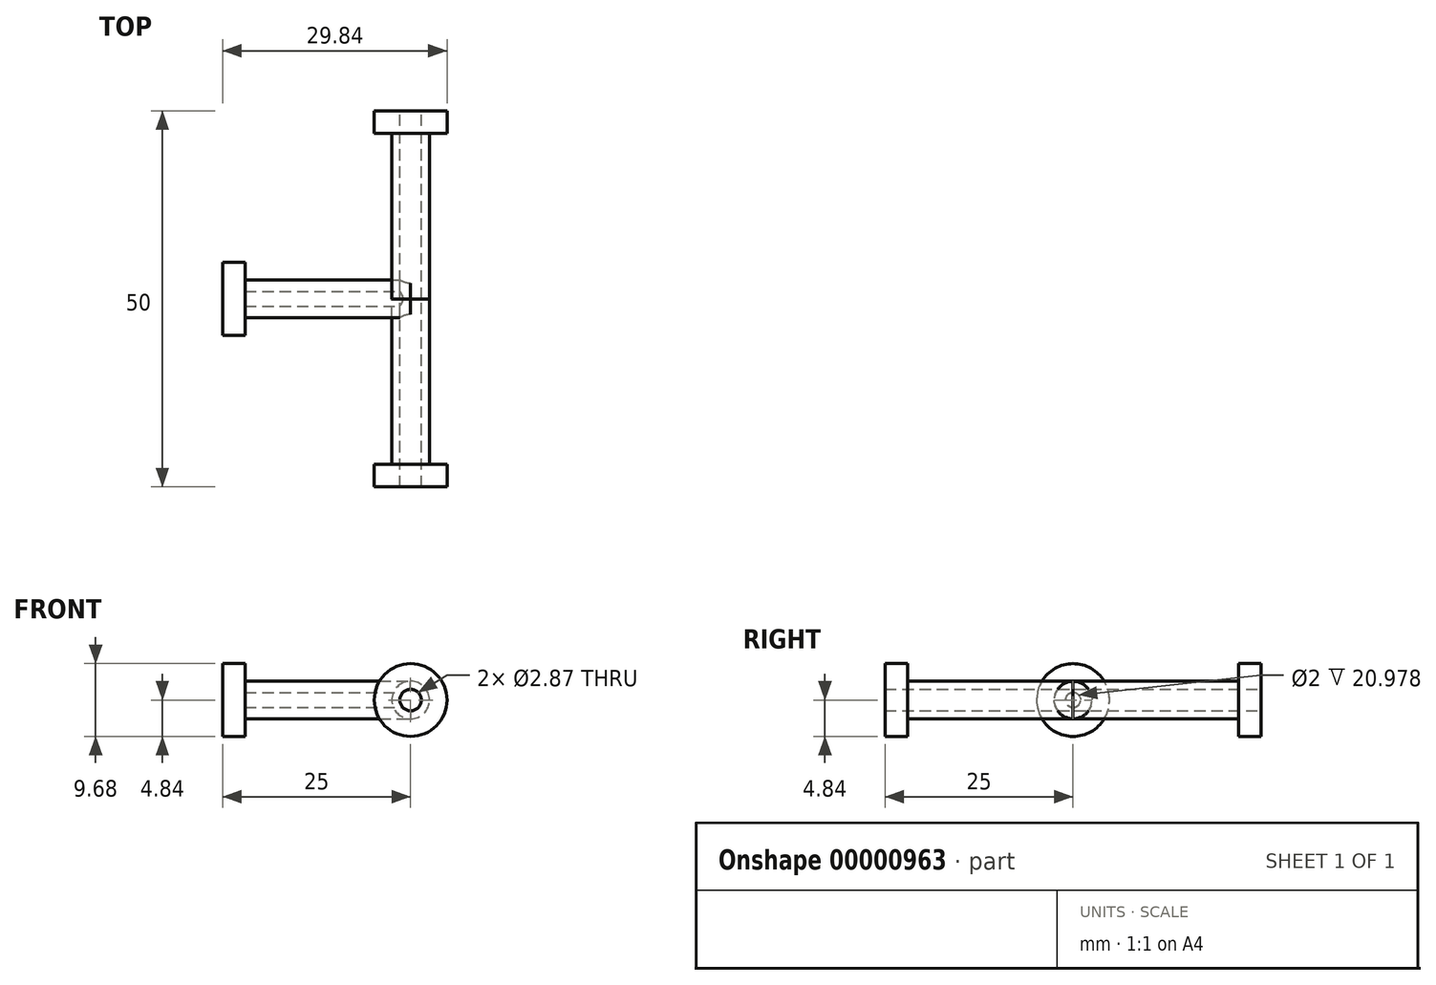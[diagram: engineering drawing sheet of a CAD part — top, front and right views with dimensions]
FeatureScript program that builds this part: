
annotation { "Feature Type Name" : "Feature", "Feature Type Description" : "" }
export const myFeature = defineFeature(function(context is Context, id is Id, definition is map)
    precondition{}
    {
        {
            var Q0;
            Q0=qCreatedBy(makeId("Front.planeOp"),FACE);
            var sketch = newSketch(context, id + "F0", { "sketchPlane" : qUnion([Q0])});
            skCircle(sketch, "E0", {"center": v(0, 0) * mm, "radius": 2.5 * mm});
            skCircle(sketch, "E1", {"center": v(0, 0) * mm, "radius": 1 * mm});
            skSolve(sketch);
        }
        {
            var Q0;
            Q0=makeQuery(id+"F0.imprint","IMPRINT",FACE,{"disambiguationData":[TD([[makeQuery(id+"F0.imprint","IMPRINT",EDGE,{"derivedFrom":sQuery(id+"F0.wireOp",EDGE,"E0")}),1.0]])]});
            extrude(context, id + "F1", {"entities" : qUnion([Q0]), "depth" : 25 * mm});
        }
        {
            var Q0;
            Q0=makeQuery(id+"F1.opExtrude","CAP_FACE",FACE,{"disambiguationData":[OSD([sQuery(id+"F0.wireOp",EDGE,"E0"),sQuery(id+"F0.wireOp",EDGE,"E1")])],"isStart":false});
            var sketch = newSketch(context, id + "F2", { "sketchPlane" : qUnion([Q0])});
            skCircle(sketch, "E2", {"center": v(0, 0) * mm, "radius": 4.84 * mm});
            skSolve(sketch);
        }
        {
            var Q0;
            Q0 = qSketchRegion(id + "F2", true);
            extrude(context, id + "F3", {"entities" : qUnion([Q0]), "operationType" : NewBodyOperationType.ADD, "oppositeDirection" : true, "depth" : 3 * mm});
        }
        {
            var Q0;
            Q0=makeQuery(id+"F1.opExtrude","SWEPT_BODY",BODY,{"disambiguationData":[OSD([sQuery(id+"F0.wireOp",EDGE,"E0"),sQuery(id+"F0.wireOp",EDGE,"E1")])]});
            var Q1;
            Q1=qCreatedBy(makeId("Front.planeOp"),FACE);
            mirror(context, id + "F4", {"entities" : qUnion([Q0]), "mirrorPlane" : qUnion([Q1])});
        }
        {
            var Q0;
            Q0=qCreatedBy(makeId("Front.planeOp"),FACE);
            var sketch = newSketch(context, id + "F5", { "sketchPlane" : qUnion([Q0])});
            skLineSegment(sketch, "E3", {"start": v(0, 0) * mm, "end": v(0, -49) * mm});
            skSolve(sketch);
        }
        {
            var Q0;
            Q0=makeQuery(id+"F1.opExtrude","SWEPT_BODY",BODY,{"disambiguationData":[OSD([sQuery(id+"F0.wireOp",EDGE,"E0"),sQuery(id+"F0.wireOp",EDGE,"E1")])]});
            var Q1;
            Q1=sQuery(id+"F5.wireOp",EDGE,"E3");
            transform(context, id + "F6", {"entities" : qUnion([Q0]), "transformType" : TransformType.ROTATION, "transformAxis" : qUnion([Q1]), "angle" : 90 * degree, "oppositeX" : false, "oppositeY" : false, "oppositeZ" : false, "makeCopy" : true});
        }
        {
            var Q0;
            Q0=makeQuery(id+"F4.opPattern","COPY",FACE,{"derivedFrom":makeQuery(id+"F3.boolean.opBoolean","MERGE",FACE,{"derivedFrom":[makeQuery(id+"F1.opExtrude","CAP_FACE",FACE,{"disambiguationData":[OSD([sQuery(id+"F0.wireOp",EDGE,"E0"),sQuery(id+"F0.wireOp",EDGE,"E1")])],"isStart":false}),makeQuery(id+"F3.opExtrude","CAP_FACE",FACE,{"disambiguationData":[OSD([sQuery(id+"F2.wireOp",EDGE,"E2")])],"isStart":true})]}),"instanceName":"1"});
            var sketch = newSketch(context, id + "F7", { "sketchPlane" : qUnion([Q0])});
            skCircle(sketch, "E4", {"center": v(0, 0) * mm, "radius": 1.43 * mm});
            skSolve(sketch);
        }
        {
            var Q0;
            Q0 = qSketchRegion(id + "F7", true);
            extrude(context, id + "F8", {"entities" : qUnion([Q0]), "operationType" : NewBodyOperationType.REMOVE, "endBound" : BoundingType.THROUGH_ALL, "oppositeDirection" : true, "depth" : 25 * mm});
        }
    });
